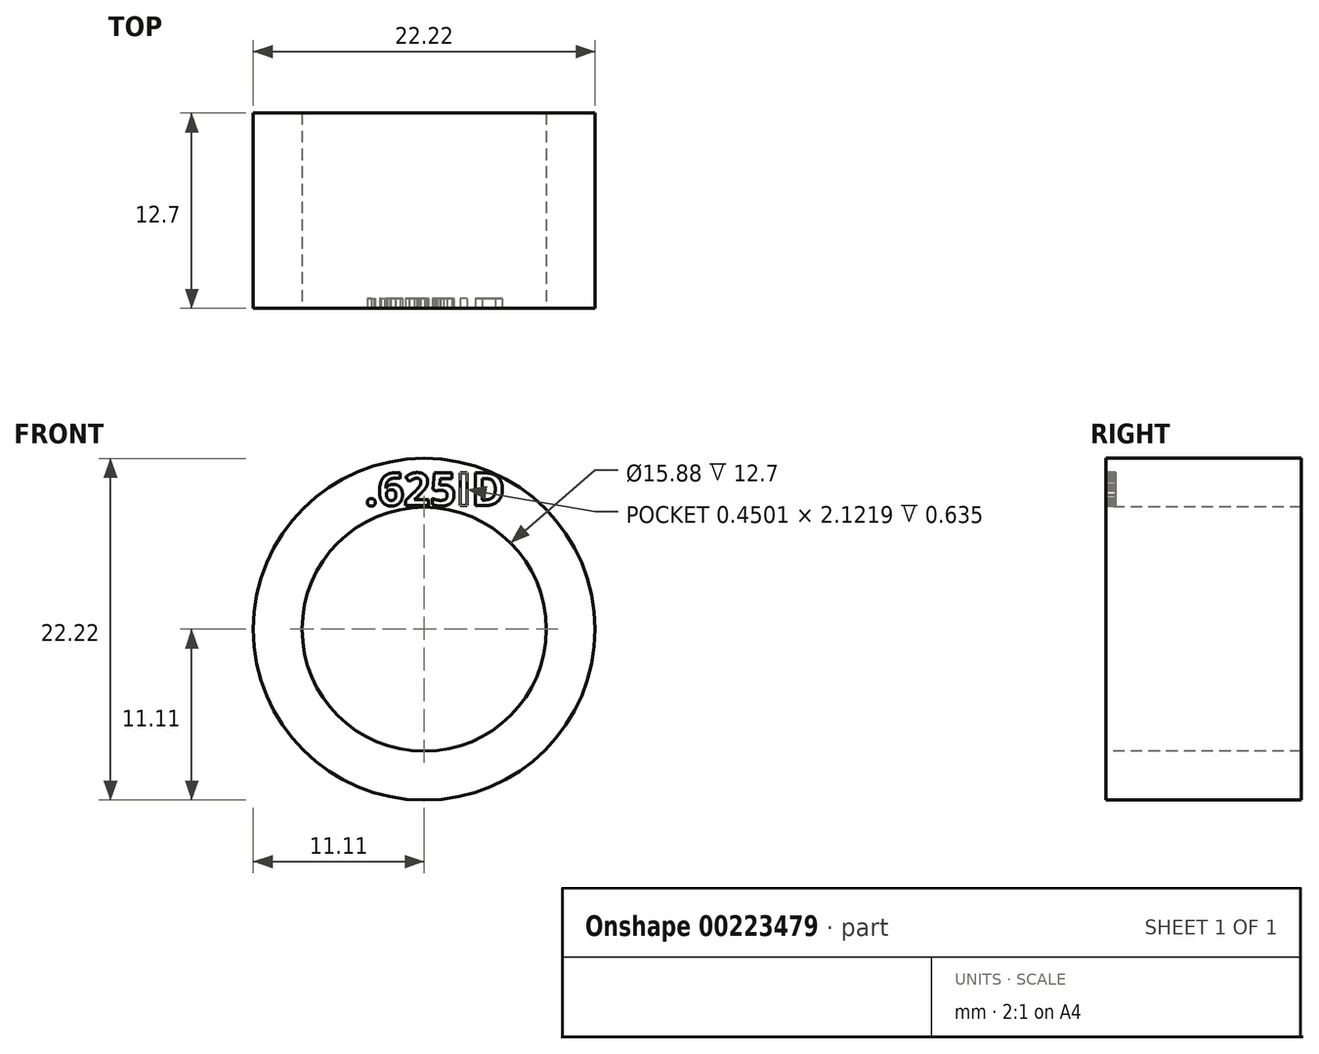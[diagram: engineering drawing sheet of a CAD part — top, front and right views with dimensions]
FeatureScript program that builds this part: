
annotation { "Feature Type Name" : "Feature", "Feature Type Description" : "" }
export const myFeature = defineFeature(function(context is Context, id is Id, definition is map)
    precondition{}
    {
        {
            var Q0;
            Q0=qCreatedBy(makeId("Front.planeOp"),FACE);
            var sketch = newSketch(context, id + "F0", { "sketchPlane" : qUnion([Q0])});
            skCircle(sketch, "E0", {"center": v(0, 0) * mm, "radius": 7.94 * mm});
            skCircle(sketch, "E1", {"center": v(0, 0) * mm, "radius": 11.11 * mm});
            skSolve(sketch);
        }
        {
            var Q0;
            Q0 = qSketchRegion(id + "F0", true);
            extrude(context, id + "F1", {"entities" : qUnion([Q0]), "oppositeDirection" : true, "depth" : 12.7 * mm});
        }
        {
            var Q0;
            Q0=makeQuery(id+"F1.opExtrude","CAP_FACE",FACE,{"disambiguationData":[OSD([sQuery(id+"F0.wireOp",EDGE,"E0"),sQuery(id+"F0.wireOp",EDGE,"E1")])],"isStart":true});
            var sketch = newSketch(context, id + "F2", { "sketchPlane" : qUnion([Q0])});
            skText(sketch, "E2", { "text": ".625ID", "fontName": "OpenSans-Bold.ttf"});
            const initialGuessF2  = {"E2": [-0.00386, 0.00804, 1, 0, 0.00214]};
            skSetInitialGuess(sketch, initialGuessF2);
            skSolve(sketch);
        }
        {
            var Q0;
            Q0 = qSketchRegion(id + "F2", true);
            extrude(context, id + "F3", {"entities" : qUnion([Q0]), "operationType" : NewBodyOperationType.REMOVE, "oppositeDirection" : true, "depth" : 0.64 * mm});
        }
    });
